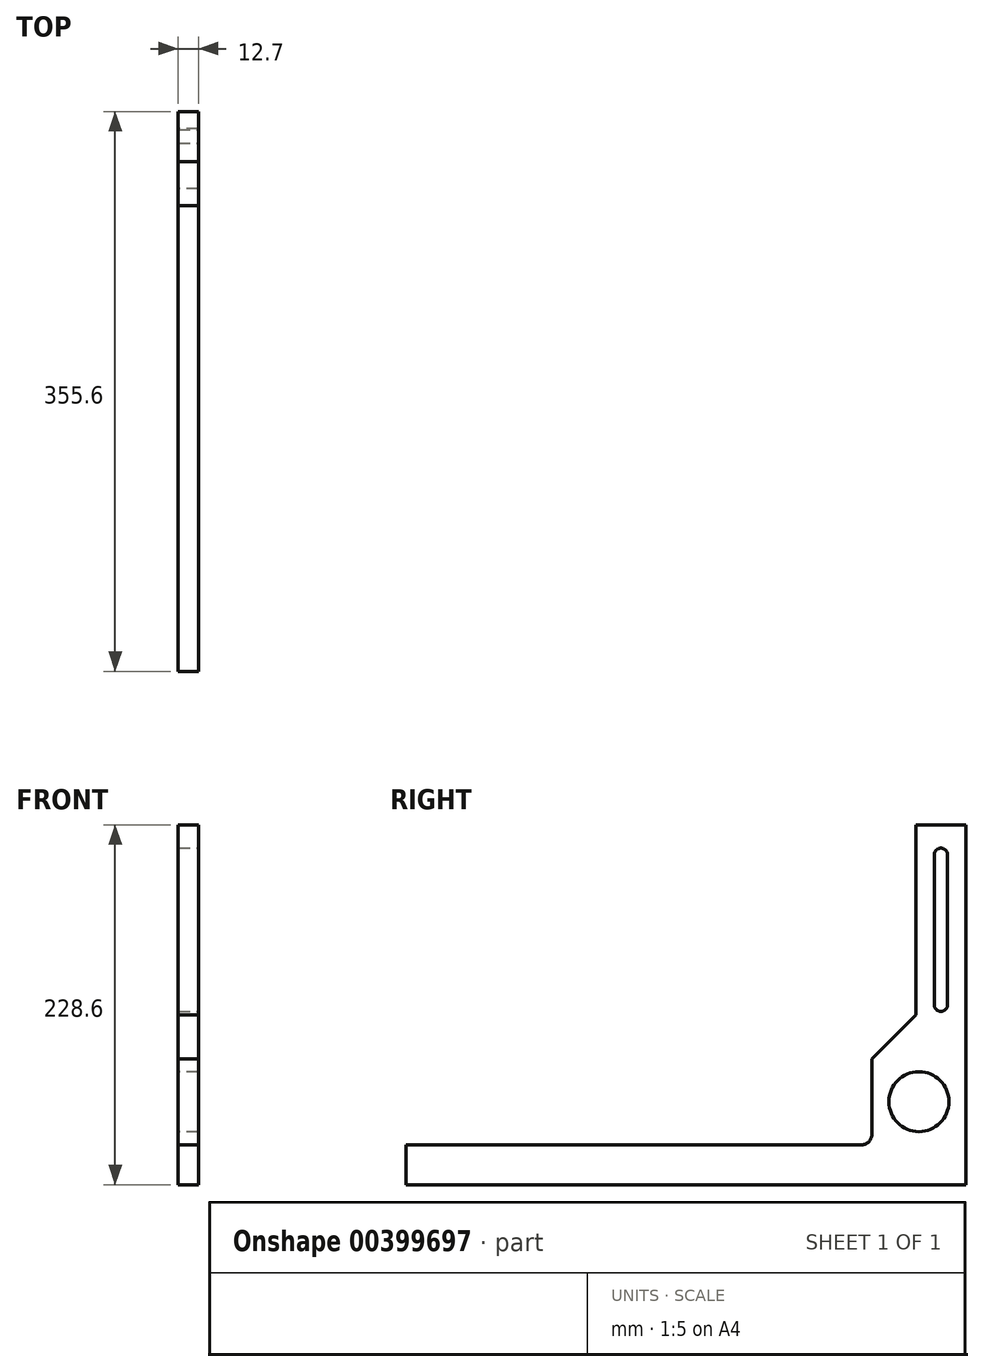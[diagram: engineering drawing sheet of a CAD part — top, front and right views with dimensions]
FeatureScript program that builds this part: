
annotation { "Feature Type Name" : "Feature", "Feature Type Description" : "" }
export const myFeature = defineFeature(function(context is Context, id is Id, definition is map)
    precondition{}
    {
        {
            var Q0;
            Q0=qCreatedBy(makeId("Right.planeOp"),FACE);
            var sketch = newSketch(context, id + "F0", { "sketchPlane" : qUnion([Q0])});
            skLineSegment(sketch, "E0.bottom", {"start": v(-177.8, 25.4) * mm, "end": v(111.75, 25.4) * mm});
            skLineSegment(sketch, "E0.top", {"start": v(-177.8, 0) * mm, "end": v(177.8, 0) * mm});
            skLineSegment(sketch, "E0.left", {"start": v(-177.8, 25.4) * mm, "end": v(-177.8, 0) * mm});
            skLineSegment(sketch, "E0.right", {"start": v(177.8, 25.4) * mm, "end": v(177.8, 0) * mm});
            skLineSegment(sketch, "E1.bottom", {"start": v(177.8, 0) * mm, "end": v(146.05, 0) * mm});
            skLineSegment(sketch, "E1.top", {"start": v(177.8, 228.6) * mm, "end": v(146.05, 228.6) * mm});
            skLineSegment(sketch, "E1.left", {"start": v(177.8, 0) * mm, "end": v(177.8, 228.6) * mm});
            skLineSegment(sketch, "E1.right", {"start": v(146.05, 107.95) * mm, "end": v(146.05, 228.6) * mm});
            skLineSegment(sketch, "E2", {"start": v(146.05, 107.95) * mm, "end": v(118.1, 80) * mm});
            skLineSegment(sketch, "E3", {"start": v(118.1, 80) * mm, "end": v(118.1, 31.75) * mm});
            skCircle(sketch, "E4", {"center": v(147.95, 52.7) * mm, "radius": 19.05 * mm});
            skPoint(sketch, "E4.centerSnap0", {"position": v(118.1, 52.7) * mm});
            skPoint(sketch, "E5.newPointB", {"position": v(118.1, 25.4) * mm});
            skArc(sketch, "E5.filletArc", {"start": v(111.75, 25.4) * mm, "mid": v(116.24, 27.26) * mm, "end": v(118.1, 31.75) * mm});
            skSolve(sketch);
        }
        {
            var Q0;
            {var subQ1=sQuery(id+"F0.wireOp",EDGE,"E0.top");Q0=makeQuery(id+"F0.imprint","IMPRINT",FACE,{"disambiguationData":[TD([[makeQuery(id+"F0.imprint","IMPRINT",EDGE,{"derivedFrom":subQ1}),1.0]])]});}
            var Q1;
            {var subQ4=sQuery(id+"F0.wireOp",EDGE,"5NJerZvU-4ijE-njmN-gXVe-Au76n7B5y2TL");Q1=makeQuery(id+"F0.imprint","IMPRINT",FACE,{"disambiguationData":[TD([[makeQuery(id+"F0.imprint","IMPRINT",EDGE,{"derivedFrom":subQ4}),1.0]])]});}
            var Q2;
            {var subQ6=sQuery(id+"F0.wireOp",EDGE,"E1.top");Q2=makeQuery(id+"F0.imprint","IMPRINT",FACE,{"disambiguationData":[TD([[makeQuery(id+"F0.imprint","IMPRINT",EDGE,{"derivedFrom":subQ6}),1.0]])]});}
            var Q3;
            {var subQ5=sQuery(id+"F0.wireOp",EDGE,"E1.bottom");Q3=makeQuery(id+"F0.imprint","IMPRINT",FACE,{"disambiguationData":[TD([[makeQuery(id+"F0.imprint","IMPRINT",EDGE,{"derivedFrom":subQ5}),-1.0]])]});}
            extrude(context, id + "F1", {"entities" : qUnion([Q0, Q1, Q2, Q3]), "depth" : 12.7 * mm});
        }
        {
            var Q0;
            Q0=makeQuery(id+"F1.opExtrude","CAP_FACE",FACE,{"disambiguationData":[OSD([sQuery(id+"F0.wireOp",EDGE,"E0.bottom"),sQuery(id+"F0.wireOp",EDGE,"E0.top"),sQuery(id+"F0.wireOp",EDGE,"E0.left"),sQuery(id+"F0.wireOp",EDGE,"E1.bottom"),sQuery(id+"F0.wireOp",EDGE,"E1.top"),sQuery(id+"F0.wireOp",EDGE,"E1.left"),sQuery(id+"F0.wireOp",EDGE,"E1.right"),sQuery(id+"F0.wireOp",EDGE,"5NJerZvU-4ijE-njmN-gXVe-Au76n7B5y2TL"),sQuery(id+"F0.wireOp",EDGE,"MKZTKdPD-a2mB-ArSv-K4fk-C1lb7IpamliS"),sQuery(id+"F0.wireOp",EDGE,"18687770-11ee-4e68-b4c8-8ee9177506a8.filletArc")])],"isStart":false});
            var sketch = newSketch(context, id + "F2", { "sketchPlane" : qUnion([Q0])});
            skLineSegment(sketch, "E6", {"start": v(161.92, 228.6) * mm, "end": v(161.92, 0) * mm, "construction": true});
            skLineSegment(sketch, "E7", {"start": v(157.7, 209.55) * mm, "end": v(157.7, 114.3) * mm});
            skLineSegment(sketch, "E8", {"start": v(166.14, 114.3) * mm, "end": v(166.14, 209.55) * mm});
            skArc(sketch, "E9", {"start": v(166.14, 114.3) * mm, "mid": v(161.93, 110.08) * mm, "end": v(157.7, 114.3) * mm});
            skArc(sketch, "E10", {"start": v(166.14, 209.55) * mm, "mid": v(161.92, 213.77) * mm, "end": v(157.7, 209.55) * mm});
            skSolve(sketch);
        }
        {
            var Q0;
            Q0=makeQuery(id+"F2.imprint","IMPRINT",FACE,{"disambiguationData":[TD([[makeQuery(id+"F2.imprint","IMPRINT",EDGE,{"derivedFrom":sQuery(id+"F2.wireOp",EDGE,"E7")}),1.0]])]});
            extrude(context, id + "F3", {"entities" : qUnion([Q0]), "operationType" : NewBodyOperationType.REMOVE, "endBound" : BoundingType.THROUGH_ALL, "oppositeDirection" : true, "depth" : 25.4 * mm});
        }
    });
